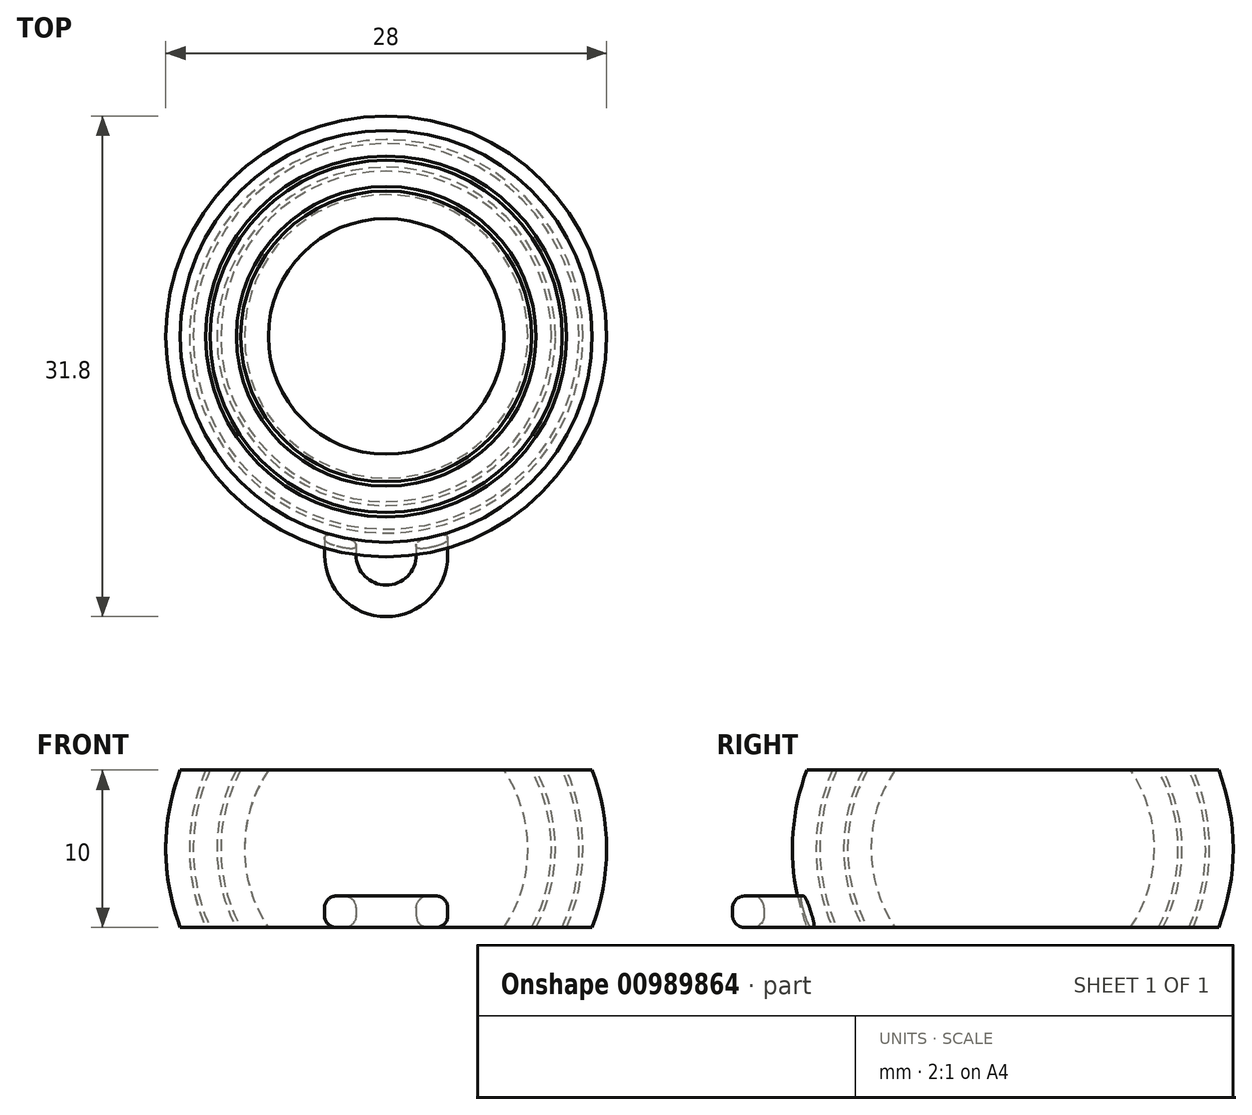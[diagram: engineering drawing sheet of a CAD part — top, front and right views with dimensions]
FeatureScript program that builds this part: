
annotation { "Feature Type Name" : "Feature", "Feature Type Description" : "" }
export const myFeature = defineFeature(function(context is Context, id is Id, definition is map)
    precondition{}
    {
        {
            var Q0;
            Q0=qCreatedBy(makeId("Front.planeOp"),FACE);
            var sketch = newSketch(context, id + "F0", { "sketchPlane" : qUnion([Q0])});
            skLineSegment(sketch, "E0", {"start": v(0, 0) * mm, "end": v(0, 10) * mm, "construction": true});
            skPoint(sketch, "E1", {"position": v(0, 5) * mm});
            skArc(sketch, "E2", {"start": v(-7.48, 10) * mm, "mid": v(-9, 5) * mm, "end": v(-7.48, 0) * mm});
            skArc(sketch, "E3.0", {"start": v(-9.23, 10) * mm, "mid": v(-10.5, 5) * mm, "end": v(-9.23, 0) * mm});
            skArc(sketch, "E4.0", {"start": v(-9.52, 10) * mm, "mid": v(-10.75, 5) * mm, "end": v(-9.52, 0) * mm});
            skArc(sketch, "E5.0", {"start": v(-11.18, 10) * mm, "mid": v(-12.25, 5) * mm, "end": v(-11.18, 0) * mm});
            skArc(sketch, "E6.0", {"start": v(-11.46, 10) * mm, "mid": v(-12.5, 5) * mm, "end": v(-11.46, 0) * mm});
            skArc(sketch, "E7.0", {"start": v(-13.08, 10) * mm, "mid": v(-14, 5) * mm, "end": v(-13.08, 0) * mm});
            skLineSegment(sketch, "E8", {"start": v(-13.08, 10) * mm, "end": v(-7.48, 10) * mm});
            skLineSegment(sketch, "E9.trimOffspring", {"start": v(-7.48, 0) * mm, "end": v(-13.08, 0) * mm});
            skSolve(sketch);
        }
        {
            var Q0;
            {var subQ0=sQuery(id+"F0.wireOp",EDGE,"E6.0");Q0=makeQuery(id+"F0.imprint","IMPRINT",FACE,{"disambiguationData":[TD([[makeQuery(id+"F0.imprint","IMPRINT",EDGE,{"derivedFrom":subQ0}),-1.0]])]});}
            var Q1;
            {var subQ0=sQuery(id+"F0.wireOp",EDGE,"E4.0");Q1=makeQuery(id+"F0.imprint","IMPRINT",FACE,{"disambiguationData":[TD([[makeQuery(id+"F0.imprint","IMPRINT",EDGE,{"derivedFrom":subQ0}),-1.0]])]});}
            var Q2;
            {var subQ0=sQuery(id+"F0.wireOp",EDGE,"E2");Q2=makeQuery(id+"F0.imprint","IMPRINT",FACE,{"disambiguationData":[TD([[makeQuery(id+"F0.imprint","IMPRINT",EDGE,{"derivedFrom":subQ0}),-1.0]])]});}
            var Q3;
            Q3=sQuery(id+"F0.wireOp",EDGE,"E0");
            revolve(context, id + "F1", {"surfaceOperationType" : NewSurfaceOperationType.NEW, "entities" : qUnion([Q0, Q1, Q2]), "axis" : qUnion([Q3]), "revolveType" : RevolveType.FULL});
        }
        {
            var Q0;
            {var subQ0=sQuery(id+"F0.wireOp",EDGE,"E9.trimOffspring");Q0=makeQuery(id+"F1.opRevolve","SWEPT_FACE",FACE,{"disambiguationData":[OSD([subQ0]),TDD([makeQuery(id+"F0.imprint","IMPRINT",EDGE,{"disambiguationData":[TD([[makeQuery(id+"F0.imprint","INTERSECT",VERTEX,{"derivedFrom":[sQuery(id+"F0.wireOp",EDGE,"E6.0"),subQ0]}),-1.0]])],"derivedFrom":subQ0})])]});}
            var sketch = newSketch(context, id + "F2", { "sketchPlane" : qUnion([Q0])});
            skLineSegment(sketch, "E10", {"start": v(0, 13.08) * mm, "end": v(0, 13.89) * mm, "construction": true});
            skLineSegment(sketch, "E11", {"start": v(-3.91, 12.48) * mm, "end": v(-3.91, 13.89) * mm});
            skArc(sketch, "E12", {"start": v(-3.91, 13.89) * mm, "mid": v(-2.77, 16.65) * mm, "end": v(0, 17.8) * mm});
            skArc(sketch, "E13.MirrorCS", {"start": v(3.91, 13.89) * mm, "mid": v(2.77, 16.65) * mm, "end": v(0, 17.8) * mm});
            skLineSegment(sketch, "E14.MirrorCS", {"start": v(3.91, 12.48) * mm, "end": v(3.91, 13.89) * mm});
            skLineSegment(sketch, "E15.0", {"start": v(1.91, 12.79) * mm, "end": v(1.91, 13.89) * mm});
            skArc(sketch, "E15.1", {"start": v(1.91, 13.89) * mm, "mid": v(1.35, 15.24) * mm, "end": v(0, 15.8) * mm});
            skArc(sketch, "E15.2", {"start": v(-1.91, 13.89) * mm, "mid": v(-1.35, 15.24) * mm, "end": v(0, 15.8) * mm});
            skLineSegment(sketch, "E15.3", {"start": v(-1.91, 12.79) * mm, "end": v(-1.91, 13.89) * mm});
            skSolve(sketch);
        }
        {
            var Q0;
            {var subQ1=sQuery(id+"F2.wireOp",EDGE,"E11");Q0=makeQuery(id+"F2.imprint","IMPRINT",FACE,{"disambiguationData":[TD([[makeQuery(id+"F2.imprint","IMPRINT",EDGE,{"derivedFrom":subQ1}),-1.0]])]});}
            extrude(context, id + "F3", {"entities" : qUnion([Q0]), "operationType" : NewBodyOperationType.ADD, "oppositeDirection" : true, "depth" : 2 * mm, "offsetDistance" : 25 * mm});
        }
        {
            var Q0;
            Q0=makeQuery(id+"F3.opExtrude","CAP_EDGE",EDGE,{"disambiguationData":[OSD([sQuery(id+"F2.wireOp",EDGE,"E12"),sQuery(id+"F2.wireOp",EDGE,"E13.MirrorCS")])],"isStart":false});
            var Q1;
            Q1=makeQuery(id+"F3.opExtrude","CAP_EDGE",EDGE,{"disambiguationData":[OSD([sQuery(id+"F2.wireOp",EDGE,"E15.1"),sQuery(id+"F2.wireOp",EDGE,"E15.2")])],"isStart":false});
            var Q2;
            Q2=makeQuery(id+"F3.opExtrude","CAP_EDGE",EDGE,{"disambiguationData":[OSD([sQuery(id+"F2.wireOp",EDGE,"E12"),sQuery(id+"F2.wireOp",EDGE,"E13.MirrorCS")])],"isStart":true});
            var Q3;
            Q3=makeQuery(id+"F3.opExtrude","CAP_EDGE",EDGE,{"disambiguationData":[OSD([sQuery(id+"F2.wireOp",EDGE,"E15.1"),sQuery(id+"F2.wireOp",EDGE,"E15.2")])],"isStart":true});
            fillet(context, id + "F4", {"entities" : qUnion([Q0, Q1, Q2, Q3]), "radius" : .75 * mm, "tangentPropagation" : true, "allowEdgeOverflow" : false});
        }
    });
